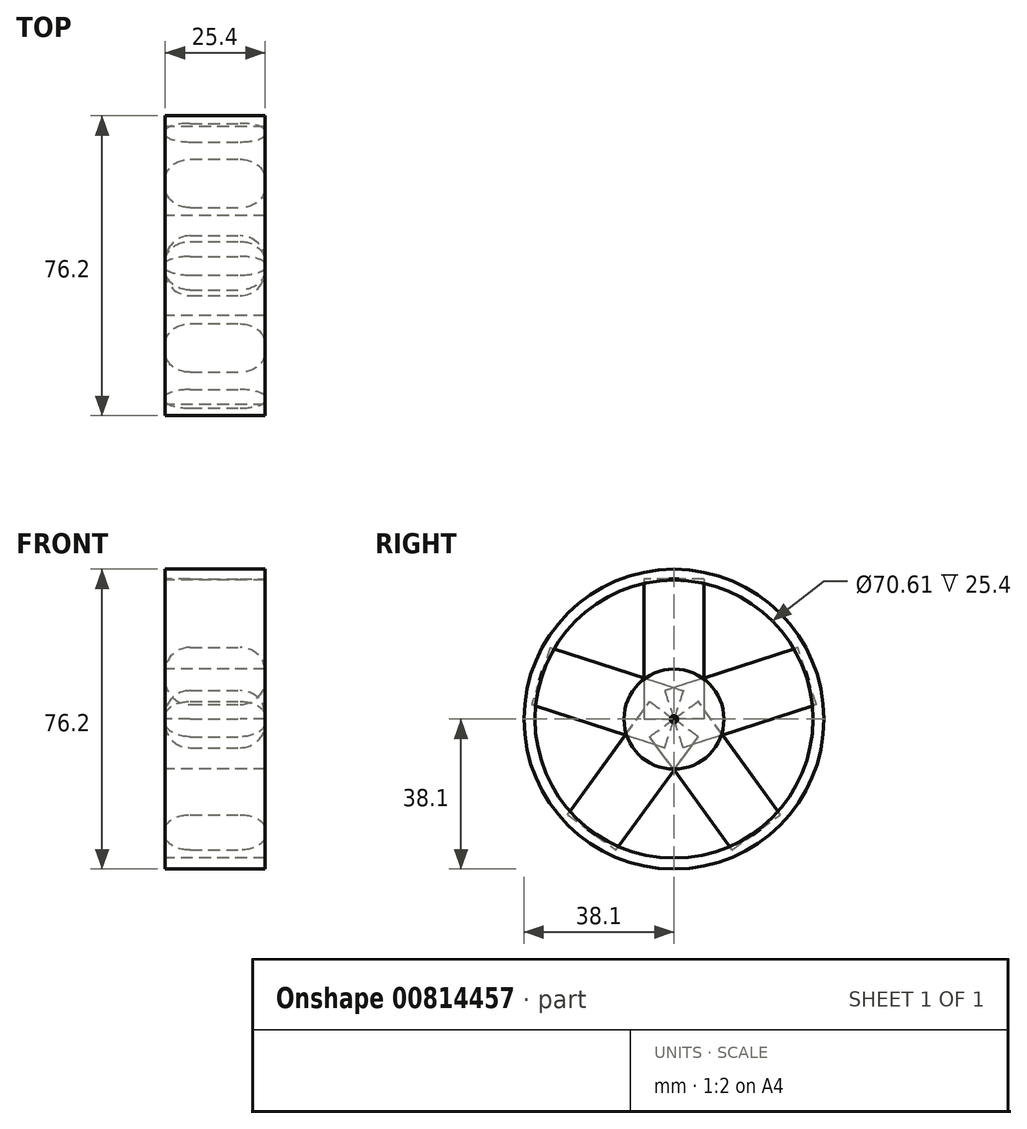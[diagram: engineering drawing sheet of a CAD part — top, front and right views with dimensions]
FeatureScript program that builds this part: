
annotation { "Feature Type Name" : "Feature", "Feature Type Description" : "" }
export const myFeature = defineFeature(function(context is Context, id is Id, definition is map)
    precondition{}
    {
        {
            var Q0;
            Q0=qCreatedBy(makeId("Right.planeOp"),FACE);
            var sketch = newSketch(context, id + "F0", { "sketchPlane" : qUnion([Q0])});
            skCircle(sketch, "E0", {"center": v(0, 0) * mm, "radius": 38.1 * mm});
            skCircle(sketch, "E1", {"center": v(0, 0) * mm, "radius": 35.3 * mm});
            skSolve(sketch);
        }
        {
            var Q0;
            Q0 = qSketchRegion(id + "F0", true);
            extrude(context, id + "F1", {"entities" : qUnion([Q0]), "depth" : 25.4 * mm, "offsetDistance" : 25.4 * mm});
        }
        {
            var Q0;
            Q0=qCreatedBy(makeId("Right.planeOp"),FACE);
            var sketch = newSketch(context, id + "F2", { "sketchPlane" : qUnion([Q0])});
            skCircle(sketch, "E2", {"center": v(0, 0) * mm, "radius": 12.7 * mm});
            skSolve(sketch);
        }
        {
            var Q0;
            Q0 = qSketchRegion(id + "F2", true);
            extrude(context, id + "F3", {"entities" : qUnion([Q0]), "depth" : 25.4 * mm, "offsetDistance" : 25.4 * mm});
        }
        {
            var Q0;
            Q0=qCreatedBy(makeId("Top.planeOp"),FACE);
            var sketch = newSketch(context, id + "F4", { "sketchPlane" : qUnion([Q0])});
            skLineSegment(sketch, "E3.bottom", {"start": v(0, 7.62) * mm, "end": v(25.4, 7.62) * mm});
            skLineSegment(sketch, "E3.top", {"start": v(0, -7.62) * mm, "end": v(25.4, -7.62) * mm});
            skLineSegment(sketch, "E3.left", {"start": v(0, 7.62) * mm, "end": v(0, -7.62) * mm});
            skLineSegment(sketch, "E3.right", {"start": v(25.4, 7.62) * mm, "end": v(25.4, -7.62) * mm});
            skSolve(sketch);
        }
        {
            var Q0;
            Q0 = qSketchRegion(id + "F4", true);
            extrude(context, id + "F5", {"entities" : qUnion([Q0]), "depth" : 35.56 * mm, "offsetDistance" : 25.4 * mm});
        }
        {
            var Q0;
            Q0=makeQuery(id+"F5.opExtrude","SWEPT_EDGE",EDGE,{"disambiguationData":[OSD([sQuery(id+"F4.wireOp",EDGE,"E3.bottom"),sQuery(id+"F4.wireOp",EDGE,"E3.right")])]});
            var Q1;
            Q1=makeQuery(id+"F5.opExtrude","SWEPT_EDGE",EDGE,{"disambiguationData":[OSD([sQuery(id+"F4.wireOp",EDGE,"E3.top"),sQuery(id+"F4.wireOp",EDGE,"E3.right")])]});
            var Q2;
            Q2=makeQuery(id+"F5.opExtrude","SWEPT_EDGE",EDGE,{"disambiguationData":[OSD([sQuery(id+"F4.wireOp",EDGE,"E3.top"),sQuery(id+"F4.wireOp",EDGE,"E3.left")])]});
            var Q3;
            Q3=makeQuery(id+"F5.opExtrude","SWEPT_EDGE",EDGE,{"disambiguationData":[OSD([sQuery(id+"F4.wireOp",EDGE,"E3.bottom"),sQuery(id+"F4.wireOp",EDGE,"E3.left")])]});
            fillet(context, id + "F6", {"entities" : qUnion([Q0, Q1, Q2, Q3]), "radius" : 6.35 * mm, "tangentPropagation" : true, "allowEdgeOverflow" : false});
        }
        {
            var Q0;
            Q0=makeQuery(id+"F5.opExtrude","SWEPT_BODY",BODY,{"disambiguationData":[OSD([sQuery(id+"F4.wireOp",EDGE,"E3.bottom"),sQuery(id+"F4.wireOp",EDGE,"E3.top"),sQuery(id+"F4.wireOp",EDGE,"E3.left"),sQuery(id+"F4.wireOp",EDGE,"E3.right")])]});
            var Q1;
            Q1=makeQuery(id+"F3.opExtrude","SWEPT_FACE",FACE,{"disambiguationData":[OSD([sQuery(id+"F2.wireOp",EDGE,"E2")])]});
            circularPattern(context, id + "F7", {"entities" : qUnion([Q0]), "axis" : qUnion([Q1]), "angle" : 360 * degree, "instanceCount" : 5, "equalSpace" : true});
        }
    });
